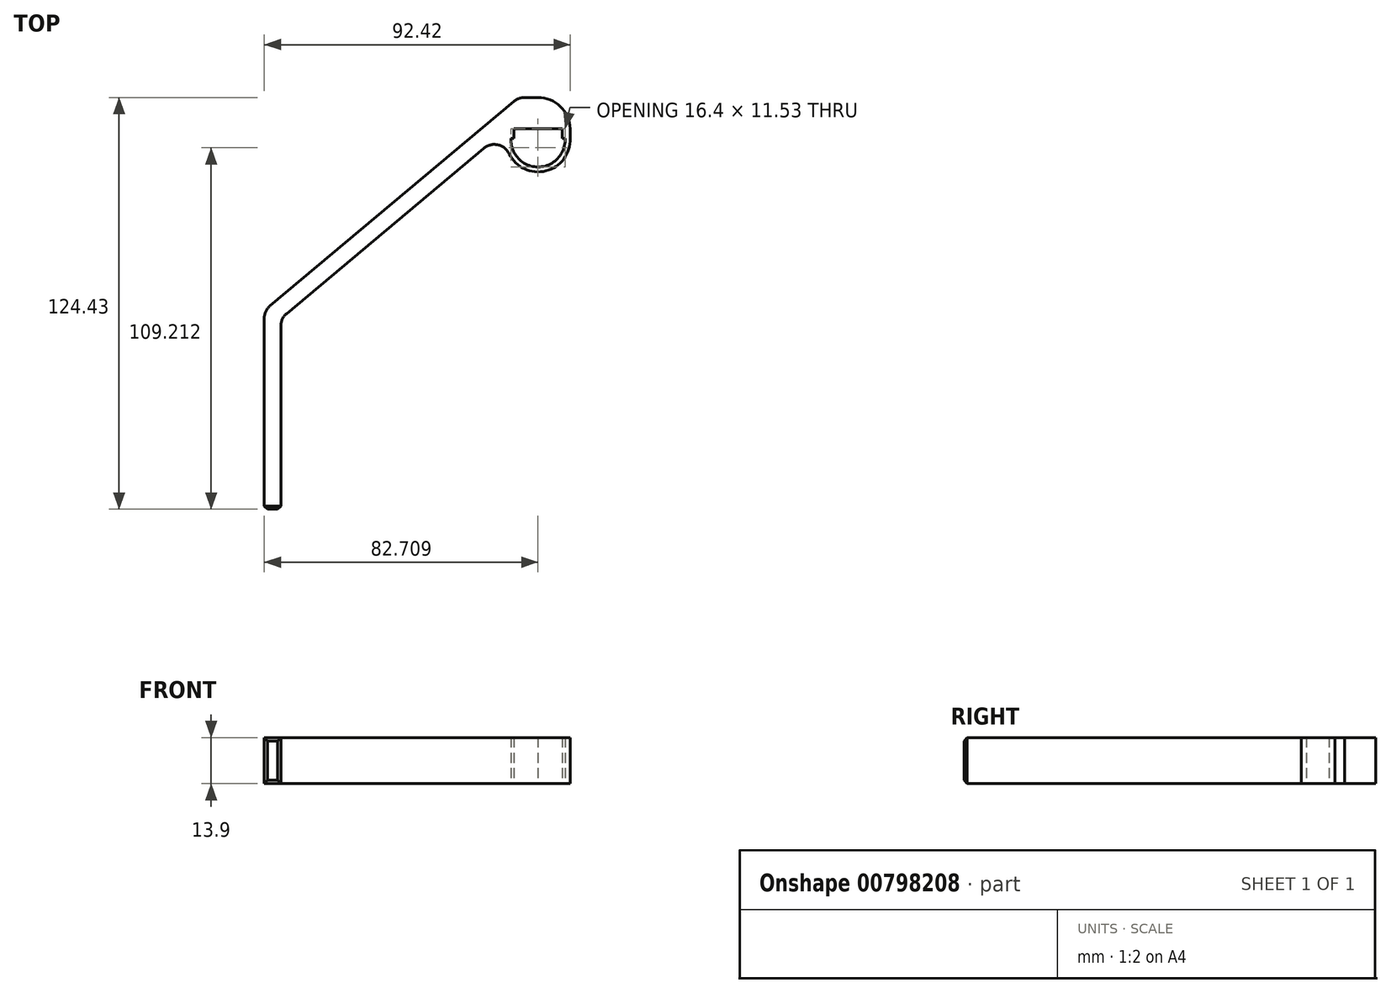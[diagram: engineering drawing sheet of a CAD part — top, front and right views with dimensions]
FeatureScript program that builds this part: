
annotation { "Feature Type Name" : "Feature", "Feature Type Description" : "" }
export const myFeature = defineFeature(function(context is Context, id is Id, definition is map)
    precondition{}
    {
        {
            var Q0;
            Q0=qCreatedBy(makeId("Top.planeOp"),FACE);
            var sketch = newSketch(context, id + "F0", { "sketchPlane" : qUnion([Q0])});
            skLineSegment(sketch, "E0", {"start": v(-18.72, -65.45) * mm, "end": v(-18.72, -5.45) * mm});
            skLineSegment(sketch, "E1", {"start": v(-18.72, -5.45) * mm, "end": v(58.07, 58.98) * mm});
            skLineSegment(sketch, "E2", {"start": v(-18.72, -65.45) * mm, "end": v(-13.72, -65.45) * mm});
            skLineSegment(sketch, "E3", {"start": v(-13.72, -65.45) * mm, "end": v(-13.72, -7.78) * mm});
            skLineSegment(sketch, "E4", {"start": v(71.29, 49.53) * mm, "end": v(56.69, 49.53) * mm});
            skLineSegment(sketch, "E5.left", {"start": v(71.29, 49.53) * mm, "end": v(71.29, 46.61) * mm});
            skLineSegment(sketch, "E5.right", {"start": v(56.69, 49.53) * mm, "end": v(56.69, 46.61) * mm});
            skLineSegment(sketch, "E6.bottom", {"start": v(55.79, 46.61) * mm, "end": v(56.69, 46.61) * mm});
            skArc(sketch, "E7", {"start": v(55.79, 46.61) * mm, "mid": v(63.99, 38) * mm, "end": v(72.19, 46.61) * mm});
            skLineSegment(sketch, "E8", {"start": v(54.29, 49.28) * mm, "end": v(54.29, 46.61) * mm});
            skLineSegment(sketch, "E9", {"start": v(73.69, 49.53) * mm, "end": v(73.69, 46.61) * mm});
            skArc(sketch, "E10", {"start": v(54.29, 46.61) * mm, "mid": v(63.99, 36.5) * mm, "end": v(73.69, 46.61) * mm});
            skLineSegment(sketch, "E11.trimOffspring", {"start": v(54.29, 49.28) * mm, "end": v(-13.72, -7.78) * mm});
            skLineSegment(sketch, "E12.trimOffspring", {"start": v(71.29, 46.61) * mm, "end": v(72.19, 46.61) * mm});
            skArc(sketch, "E13", {"start": v(73.69, 49.53) * mm, "mid": v(63.87, 58.98) * mm, "end": v(54.29, 49.28) * mm});
            skLineSegment(sketch, "E14", {"start": v(64.11, 58.98) * mm, "end": v(58.07, 58.98) * mm});
            skPoint(sketch, "E14.startSnap0", {"position": v(63.87, 58.98) * mm});
            skSolve(sketch);
        }
        {
            var Q0;
            Q0 = qSketchRegion(id + "F0", true);
            extrude(context, id + "F1", {"entities" : qUnion([Q0]), "depth" : 13.9 * mm, "offsetDistance" : 25 * mm});
        }
        {
            var Q0;
            Q0=makeQuery(id+"F1.opExtrude","SWEPT_EDGE",EDGE,{"disambiguationData":[OSD([sQuery(id+"F0.wireOp",EDGE,"E1"),sQuery(id+"F0.wireOp",EDGE,"E14")])]});
            fillet(context, id + "F2", {"entities" : qUnion([Q0]), "radius" : 5 * mm, "tangentPropagation" : true, "allowEdgeOverflow" : false});
        }
        {
            var Q0;
            Q0=makeQuery(id+"F1.opExtrude","SWEPT_EDGE",EDGE,{"disambiguationData":[OSD([sQuery(id+"F0.wireOp",EDGE,"E8"),sQuery(id+"F0.wireOp",EDGE,"E11.trimOffspring"),sQuery(id+"F0.wireOp",EDGE,"E13")])]});
            fillet(context, id + "F3", {"entities" : qUnion([Q0]), "radius" : 5 * mm, "tangentPropagation" : true, "allowEdgeOverflow" : false});
        }
        {
            var Q0;
            Q0=makeQuery(id+"F1.opExtrude","SWEPT_EDGE",EDGE,{"disambiguationData":[OSD([sQuery(id+"F0.wireOp",EDGE,"E3"),sQuery(id+"F0.wireOp",EDGE,"E11.trimOffspring")])]});
            var Q1;
            Q1=makeQuery(id+"F1.opExtrude","SWEPT_EDGE",EDGE,{"disambiguationData":[OSD([sQuery(id+"F0.wireOp",EDGE,"E0"),sQuery(id+"F0.wireOp",EDGE,"E1")])]});
            fillet(context, id + "F4", {"entities" : qUnion([Q0, Q1]), "radius" : 5 * mm, "tangentPropagation" : true, "allowEdgeOverflow" : false});
        }
        {
            var Q0;
            Q0=makeQuery(id+"F1.opExtrude","SWEPT_EDGE",EDGE,{"disambiguationData":[OSD([sQuery(id+"F0.wireOp",EDGE,"E0"),sQuery(id+"F0.wireOp",EDGE,"E2")])]});
            var Q1;
            Q1=makeQuery(id+"F1.opExtrude","CAP_EDGE",EDGE,{"disambiguationData":[OSD([sQuery(id+"F0.wireOp",EDGE,"E2")])],"isStart":false});
            var Q2;
            Q2=makeQuery(id+"F1.opExtrude","SWEPT_EDGE",EDGE,{"disambiguationData":[OSD([sQuery(id+"F0.wireOp",EDGE,"E2"),sQuery(id+"F0.wireOp",EDGE,"E3")])]});
            var Q3;
            Q3=makeQuery(id+"F1.opExtrude","CAP_EDGE",EDGE,{"disambiguationData":[OSD([sQuery(id+"F0.wireOp",EDGE,"E2")])],"isStart":true});
            chamfer(context, id + "F5", {"entities" : qUnion([Q0, Q1, Q2, Q3]), "width" : 1 * mm, "tangentPropagation" : true});
        }
    });
